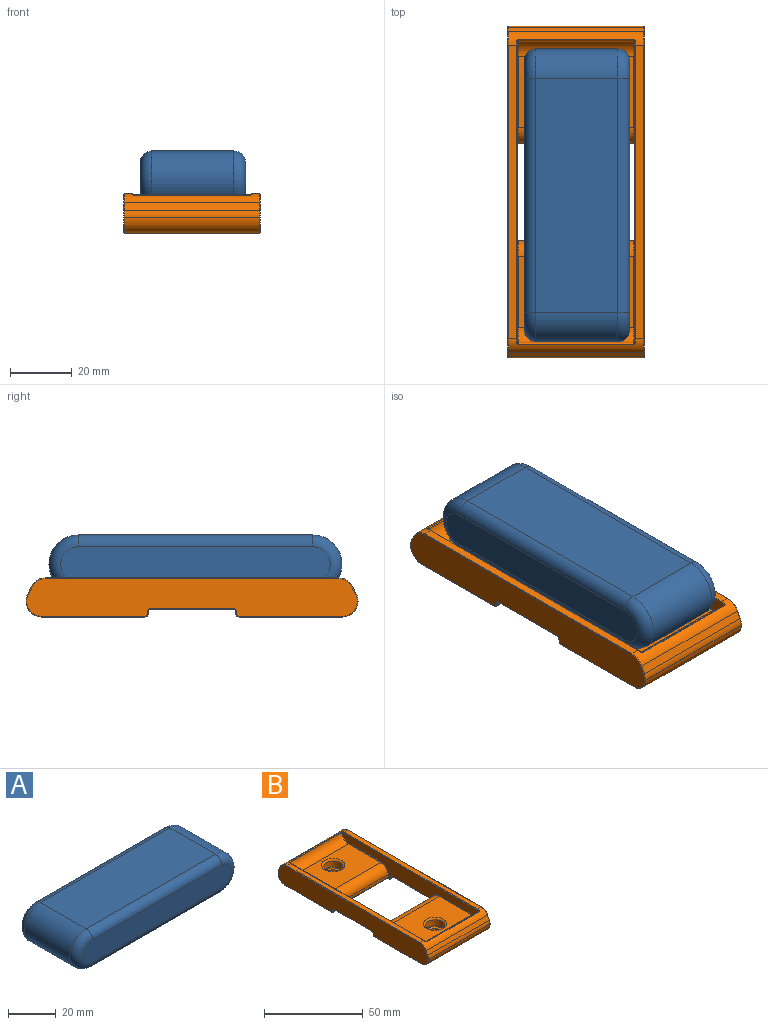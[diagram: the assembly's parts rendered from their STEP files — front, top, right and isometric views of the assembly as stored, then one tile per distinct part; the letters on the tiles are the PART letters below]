
ASSEMBLY  parts=2 mates=3
PART A: 14 faces, bbox 96.8x34.3x20.6 mm
  f0: plane 76.2x26.67mm, normal (0,0,1), area 2032.3mm2, adj f1,f3,f6,f10
  f1: cylinder r=9.53mm len=26.67mm, axis (0,1,0), area 798.1mm2, adj f0,f2,f8,f12
  f2: plane 76.2x26.67mm, normal (0,0,-1), area 2032.3mm2, adj f1,f3,f9,f13
  f3: cylinder r=9.53mm len=26.67mm, axis (0,1,0), area 798.1mm2, adj f0,f2,f7,f11
  f4: plane 87.63x11.43mm, normal (0,-1,0), area 973.6mm2, adj f10,f11,f12,f13
  f5: plane 87.63x11.43mm, normal (0,1,0), area 973.6mm2, adj f6,f7,f8,f9
  f6: cylinder r=3.81mm len=76.2mm, axis (-1,0,0), area 456mm2, adj f0,f5,f7,f8
  f7: torus R=5.71mm, axis (0,-1,0), area 153.1mm2, adj f3,f5,f6,f9
  f8: torus R=5.71mm, axis (0,-1,0), area 153.1mm2, adj f1,f5,f6,f9
  f9: cylinder r=3.81mm len=76.2mm, axis (1,0,0), area 456mm2, adj f2,f5,f7,f8
  f10: cylinder r=3.81mm len=76.2mm, axis (1,0,0), area 456mm2, adj f0,f4,f11,f12
  f11: torus R=5.71mm, axis (0,-1,0), area 153.1mm2, adj f3,f4,f10,f13
  f12: torus R=5.71mm, axis (0,-1,0), area 153.1mm2, adj f1,f4,f10,f13
  f13: cylinder r=3.81mm len=76.2mm, axis (-1,0,0), area 456mm2, adj f2,f4,f11,f12
PART B: 148 faces, bbox 44.5x108.8x13.7 mm
  f0: plane 95.32x2.67mm, normal (0,0,1), area 254.2mm2, adj f35,f36,f50,f124
  f1: plane 37.59x23.18mm, normal (0,0,1), area 762.3mm2, adj f23,f31,f49,f103,f107
  f2: plane 2.67x0.51mm, normal (0,1,0), area 1.4mm2, adj f44,f46,f65,f139
  f3: plane 2.67x0.51mm, normal (0,-1,0), area 1.4mm2, adj f45,f47,f66,f131
  f4: plane 26.54x2.67mm, normal (0,0,-1), area 70.8mm2, adj f46,f47,f69,f135
  f5: plane 43.95x33.6mm, normal (0,0,-1), area 1383.9mm2, adj f32,f38,f40,f44,f61,f81,f102,f104
  f6: plane 107.44x12.19mm, normal (1,0,0), area 1204.4mm2, adj f50,f51,f52,f53,f54,f55,f56,f57
  f7: plane 95.32x2.67mm, normal (0,0,1), area 254.2mm2, adj f35,f36,f70,f117
  f8: plane 43.94x0.07mm, normal (0,-1,0), area 3.1mm2, adj f32,f37,f57,f77
  f9: plane 43.95x33.6mm, normal (0,0,-1), area 1383.9mm2, adj f33,f39,f41,f45,f62,f82,f93,f95
  f10: plane 43.94x0.07mm, normal (0,1,0), area 3.1mm2, adj f33,f34,f58,f78
  f11: plane 43.94x2.47mm, normal (0,0.89,0.45), area 121.3mm2, adj f34,f35,f54,f74
  f12: plane 43.94x2.47mm, normal (0,-0.89,0.45), area 121.3mm2, adj f36,f37,f53,f73
  f13: plane 107.44x12.19mm, normal (-1,0,0), area 1204.4mm2, adj f70,f71,f72,f73,f74,f75,f76,f77
  f14: plane 97.88x12.19mm, normal (-1,0,0), area 614.5mm2, adj f107,f110,f111,f115,f119,f120,f124,f126
  f15: plane 97.88x12.19mm, normal (1,0,0), area 614.5mm2, adj f90,f91,f92,f93,f94,f96,f97,f98
  f16: plane 37.59x23.18mm, normal (0,0,1), area 762.3mm2, adj f24,f30,f48,f118,f134
  f17: cylinder r=2.9mm len=5.8mm, axis (0,0,1), area 43.1mm2, adj f18,f145
  f18: plane 9.24x9.24mm, normal (0,0,1), area 40.7mm2, adj f17,f146
  f19: cylinder r=4.88mm len=9.75mm, axis (0,0,1), area 114.3mm2, adj f48,f146
  f20: cylinder r=2.9mm len=5.8mm, axis (0,0,1), area 43.1mm2, adj f21,f144
  f21: plane 9.24x9.24mm, normal (0,0,1), area 40.7mm2, adj f20,f147
  f22: cylinder r=4.88mm len=9.75mm, axis (0,0,1), area 114.3mm2, adj f49,f147
  f23: cylinder r=5.08mm len=37.59mm, axis (-1,0,0), area 278.7mm2, adj f1,f105,f111,f112
  f24: cylinder r=5.08mm len=37.59mm, axis (1,0,0), area 278.7mm2, adj f16,f122,f128,f132
  f25: plane 2.67x0.51mm, normal (0,1,0), area 1.4mm2, adj f40,f43,f85,f98
  f26: plane 2.67x0.51mm, normal (0,-1,0), area 1.4mm2, adj f41,f42,f86,f90
  f27: plane 26.54x2.67mm, normal (0,0,-1), area 70.8mm2, adj f42,f43,f89,f94
  f28: plane 37.59x1.52mm, normal (0,1,0), area 57.3mm2, adj f30,f38,f109,f138
  f29: plane 37.59x1.52mm, normal (0,-1,0), area 57.3mm2, adj f31,f39,f99,f115
  f30: cylinder r=5.08mm len=37.59mm, axis (-1,0,0), area 300mm2, adj f16,f28,f114,f136
  f31: cylinder r=5.08mm len=37.59mm, axis (1,0,0), area 300mm2, adj f1,f29,f101,f110
  f32: cylinder r=5.08mm len=43.94mm, axis (-1,0,0), area 350.6mm2, adj f5,f8,f59,f79
  f33: cylinder r=5.08mm len=43.94mm, axis (-1,0,0), area 350.6mm2, adj f9,f10,f60,f80
  f34: cylinder r=5.08mm len=43.94mm, axis (-1,0,0), area 103.5mm2, adj f10,f11,f56,f76
  f35: cylinder r=5.08mm len=43.94mm, axis (-1,0,0), area 173.5mm2, adj f0,f7,f11,f52,f72,f108,f112,f113
  f36: cylinder r=5.08mm len=43.94mm, axis (-1,0,0), area 173.5mm2, adj f0,f7,f12,f51,f71,f121,f125,f127
  f37: cylinder r=5.08mm len=43.94mm, axis (-1,0,0), area 103.5mm2, adj f8,f12,f55,f75
  f38: cylinder r=1.02mm len=37.59mm, axis (1,0,0), area 60mm2, adj f5,f28,f106,f140
  f39: cylinder r=1.02mm len=37.59mm, axis (-1,0,0), area 60mm2, adj f9,f29,f97,f119
  f40: cylinder r=1.02mm len=2.67mm, axis (-1,0,0), area 4.3mm2, adj f5,f25,f83,f100
  f41: cylinder r=1.02mm len=2.67mm, axis (1,0,0), area 4.3mm2, adj f9,f26,f84,f91
  f42: cylinder r=1.02mm len=2.67mm, axis (1,0,0), area 4.3mm2, adj f26,f27,f88,f92
  f43: cylinder r=1.02mm len=2.67mm, axis (-1,0,0), area 4.3mm2, adj f25,f27,f87,f96
  f44: cylinder r=1.02mm len=2.67mm, axis (-1,0,0), area 4.3mm2, adj f2,f5,f63,f141
  f45: cylinder r=1.02mm len=2.67mm, axis (1,0,0), area 4.3mm2, adj f3,f9,f64,f129
  f46: cylinder r=1.02mm len=2.67mm, axis (-1,0,0), area 4.3mm2, adj f2,f4,f67,f137
  f47: cylinder r=1.02mm len=2.67mm, axis (1,0,0), area 4.3mm2, adj f3,f4,f68,f133
  f48: torus R=5.89mm, axis (0,0,1), area 52.6mm2, adj f16,f19
  f49: torus R=5.89mm, axis (0,0,1), area 52.6mm2, adj f1,f22
  f50: cylinder r=0.25mm len=95.32mm, axis (0,1,0), area 38mm2, adj f0,f6,f51,f52
  f51: torus R=4.83mm, axis (1,0,0), area 2.2mm2, adj f6,f36,f50,f53
  f52: torus R=4.83mm, axis (1,0,0), area 2.2mm2, adj f6,f35,f50,f54
  f53: cylinder r=0.25mm len=2.58mm, axis (0,0.45,0.89), area 1.1mm2, adj f6,f12,f51,f55
  f54: cylinder r=0.25mm len=2.58mm, axis (0,0.45,-0.89), area 1.1mm2, adj f6,f11,f52,f56
  f55: torus R=4.83mm, axis (1,0,0), area 0.9mm2, adj f6,f37,f53,f57
  f56: torus R=4.83mm, axis (1,0,0), area 0.9mm2, adj f6,f34,f54,f58
  f57: cylinder r=0.25mm len=0.25mm, axis (0,0,1), area 0mm2, adj f6,f8,f55,f59
  f58: cylinder r=0.25mm len=0.25mm, axis (0,0,-1), area 0mm2, adj f6,f10,f56,f60
  f59: torus R=4.83mm, axis (1,0,0), area 3.1mm2, adj f6,f32,f57,f61
  f60: torus R=4.83mm, axis (1,0,0), area 3.1mm2, adj f6,f33,f58,f62
  f61: cylinder r=0.25mm len=33.59mm, axis (0,-1,0), area 13.4mm2, adj f5,f6,f59,f63
  f62: cylinder r=0.25mm len=33.59mm, axis (0,-1,0), area 13.4mm2, adj f6,f9,f60,f64
  f63: torus R=0.76mm, axis (1,0,0), area 0.6mm2, adj f6,f44,f61,f65
  f64: torus R=0.76mm, axis (1,0,0), area 0.6mm2, adj f6,f45,f62,f66
  f65: cylinder r=0.25mm len=0.51mm, axis (0,0,1), area 0.2mm2, adj f2,f6,f63,f67
  f66: cylinder r=0.25mm len=0.51mm, axis (0,0,-1), area 0.2mm2, adj f3,f6,f64,f68
  f67: torus R=1.27mm, axis (1,0,0), area 0.7mm2, adj f6,f46,f65,f69
  f68: torus R=1.27mm, axis (1,0,0), area 0.7mm2, adj f6,f47,f66,f69
  f69: cylinder r=0.25mm len=26.54mm, axis (0,1,0), area 10.6mm2, adj f4,f6,f67,f68
  f70: cylinder r=0.25mm len=95.32mm, axis (0,-1,0), area 38mm2, adj f7,f13,f71,f72
  f71: torus R=4.83mm, axis (1,0,0), area 2.2mm2, adj f13,f36,f70,f73
  f72: torus R=4.83mm, axis (1,0,0), area 2.2mm2, adj f13,f35,f70,f74
  f73: cylinder r=0.25mm len=2.58mm, axis (0,-0.45,-0.89), area 1.1mm2, adj f12,f13,f71,f75
  f74: cylinder r=0.25mm len=2.58mm, axis (0,-0.45,0.89), area 1.1mm2, adj f11,f13,f72,f76
  f75: torus R=4.83mm, axis (1,0,0), area 0.9mm2, adj f13,f37,f73,f77
  f76: torus R=4.83mm, axis (1,0,0), area 0.9mm2, adj f13,f34,f74,f78
  f77: cylinder r=0.25mm len=0.25mm, axis (0,0,-1), area 0mm2, adj f8,f13,f75,f79
  f78: cylinder r=0.25mm len=0.25mm, axis (0,0,1), area 0mm2, adj f10,f13,f76,f80
  f79: torus R=4.83mm, axis (1,0,0), area 3.1mm2, adj f13,f32,f77,f81
  f80: torus R=4.83mm, axis (1,0,0), area 3.1mm2, adj f13,f33,f78,f82
  f81: cylinder r=0.25mm len=33.59mm, axis (0,1,0), area 13.4mm2, adj f5,f13,f79,f83
  f82: cylinder r=0.25mm len=33.59mm, axis (0,1,0), area 13.4mm2, adj f9,f13,f80,f84
  f83: torus R=0.76mm, axis (1,0,0), area 0.6mm2, adj f13,f40,f81,f85
  f84: torus R=0.76mm, axis (1,0,0), area 0.6mm2, adj f13,f41,f82,f86
  f85: cylinder r=0.25mm len=0.51mm, axis (0,0,-1), area 0.2mm2, adj f13,f25,f83,f87
  f86: cylinder r=0.25mm len=0.51mm, axis (0,0,1), area 0.2mm2, adj f13,f26,f84,f88
  f87: torus R=1.27mm, axis (1,0,0), area 0.7mm2, adj f13,f43,f85,f89
  f88: torus R=1.27mm, axis (1,0,0), area 0.7mm2, adj f13,f42,f86,f89
  f89: cylinder r=0.25mm len=26.54mm, axis (0,-1,0), area 10.6mm2, adj f13,f27,f87,f88
  f90: cylinder r=0.25mm len=0.51mm, axis (0,0,1), area 0.2mm2, adj f15,f26,f91,f92
  f91: torus R=0.76mm, axis (-1,0,0), area 0.6mm2, adj f15,f41,f90,f93
  f92: torus R=1.27mm, axis (-1,0,0), area 0.7mm2, adj f15,f42,f90,f94
  f93: cylinder r=0.25mm len=0.57mm, axis (0,-1,0), area 0.2mm2, adj f9,f15,f91,f95
  f94: cylinder r=0.25mm len=26.54mm, axis (0,-1,0), area 10.6mm2, adj f15,f27,f92,f96
  f95: bspline ~1.19x0.51mm, area 0.2mm2, adj f9,f93,f97
  f96: torus R=1.27mm, axis (-1,0,0), area 0.7mm2, adj f15,f43,f94,f98
  f97: torus R=1.27mm, axis (-1,0,0), area 0.4mm2, adj f15,f39,f95,f99
  f98: cylinder r=0.25mm len=0.51mm, axis (0,0,-1), area 0.2mm2, adj f15,f25,f96,f100
  f99: cylinder r=0.25mm len=1.52mm, axis (0,0,1), area 0.6mm2, adj f15,f29,f97,f101
  f100: torus R=0.76mm, axis (-1,0,0), area 0.6mm2, adj f15,f40,f98,f102
  f101: torus R=5.33mm, axis (-1,0,0), area 3.2mm2, adj f15,f31,f99,f103
  f102: cylinder r=0.25mm len=0.57mm, axis (0,-1,0), area 0.2mm2, adj f5,f15,f100,f104
  f103: cylinder r=0.25mm len=23.18mm, axis (0,-1,0), area 9.2mm2, adj f1,f15,f101,f105
  f104: bspline ~1.19x0.51mm, area 0.2mm2, adj f5,f102,f106
  f105: torus R=4.83mm, axis (-1,0,0), area 2.9mm2, adj f15,f23,f103,f108
  f106: torus R=1.27mm, axis (-1,0,0), area 0.4mm2, adj f15,f38,f104,f109
  f107: cylinder r=0.25mm len=23.18mm, axis (0,1,0), area 9.2mm2, adj f1,f14,f110,f111
  f108: bspline ~0.64x0.6mm, area 0.2mm2, adj f35,f105,f112,f113
  f109: cylinder r=0.25mm len=1.52mm, axis (0,0,-1), area 0.6mm2, adj f15,f28,f106,f114
  f110: torus R=5.33mm, axis (-1,0,0), area 3.2mm2, adj f14,f31,f107,f115
  f111: torus R=4.83mm, axis (-1,0,0), area 2.9mm2, adj f14,f23,f107,f116
  f112: cylinder r=0.25mm len=37.59mm, axis (1,0,0), area 17.5mm2, adj f23,f35,f108,f116
  f113: torus R=4.83mm, axis (-1,0,0), area 0.5mm2, adj f15,f35,f108,f117
  f114: torus R=5.33mm, axis (-1,0,0), area 3.2mm2, adj f15,f30,f109,f118
  f115: cylinder r=0.25mm len=1.52mm, axis (0,0,-1), area 0.6mm2, adj f14,f29,f110,f119
  f116: bspline ~0.63x0.62mm, area 0.2mm2, adj f35,f111,f112,f120
  f117: cylinder r=0.25mm len=95.32mm, axis (0,-1,0), area 38mm2, adj f7,f15,f113,f121
  f118: cylinder r=0.25mm len=23.18mm, axis (0,-1,0), area 9.2mm2, adj f15,f16,f114,f122
  f119: torus R=1.27mm, axis (-1,0,0), area 0.4mm2, adj f14,f39,f115,f123
  f120: torus R=4.83mm, axis (-1,0,0), area 0.5mm2, adj f14,f35,f116,f124
  f121: torus R=4.83mm, axis (-1,0,0), area 0.5mm2, adj f15,f36,f117,f125
  f122: torus R=4.83mm, axis (-1,0,0), area 2.9mm2, adj f15,f24,f118,f125
  f123: bspline ~1.19x0.51mm, area 0.2mm2, adj f9,f119,f126
  f124: cylinder r=0.25mm len=95.32mm, axis (0,1,0), area 38mm2, adj f0,f14,f120,f127
  f125: bspline ~0.63x0.62mm, area 0.2mm2, adj f36,f121,f122,f128
  f126: cylinder r=0.25mm len=0.57mm, axis (0,1,0), area 0.2mm2, adj f9,f14,f123,f129
  f127: torus R=4.83mm, axis (-1,0,0), area 0.5mm2, adj f14,f36,f124,f130
  f128: cylinder r=0.25mm len=37.59mm, axis (-1,0,0), area 17.5mm2, adj f24,f36,f125,f130
  f129: torus R=0.76mm, axis (-1,0,0), area 0.6mm2, adj f14,f45,f126,f131
  f130: bspline ~0.64x0.6mm, area 0.2mm2, adj f36,f127,f128,f132
  f131: cylinder r=0.25mm len=0.51mm, axis (0,0,-1), area 0.2mm2, adj f3,f14,f129,f133
  f132: torus R=4.83mm, axis (-1,0,0), area 2.9mm2, adj f14,f24,f130,f134
  f133: torus R=1.27mm, axis (-1,0,0), area 0.7mm2, adj f14,f47,f131,f135
  f134: cylinder r=0.25mm len=23.18mm, axis (0,1,0), area 9.2mm2, adj f14,f16,f132,f136
  f135: cylinder r=0.25mm len=26.54mm, axis (0,1,0), area 10.6mm2, adj f4,f14,f133,f137
  f136: torus R=5.33mm, axis (-1,0,0), area 3.2mm2, adj f14,f30,f134,f138
  f137: torus R=1.27mm, axis (-1,0,0), area 0.7mm2, adj f14,f46,f135,f139
  f138: cylinder r=0.25mm len=1.52mm, axis (0,0,1), area 0.6mm2, adj f14,f28,f136,f140
  f139: cylinder r=0.25mm len=0.51mm, axis (0,0,1), area 0.2mm2, adj f2,f14,f137,f141
  f140: torus R=1.27mm, axis (-1,0,0), area 0.4mm2, adj f14,f38,f138,f142
  f141: torus R=0.76mm, axis (-1,0,0), area 0.6mm2, adj f14,f44,f139,f143
  f142: bspline ~1.19x0.51mm, area 0.2mm2, adj f5,f140,f143
  f143: cylinder r=0.25mm len=0.57mm, axis (0,1,0), area 0.2mm2, adj f5,f14,f141,f142
  f144: torus R=3.15mm, axis (0,0,1), area 7.5mm2, adj f9,f20
  f145: torus R=3.15mm, axis (0,0,1), area 7.5mm2, adj f5,f17
  f146: torus R=4.62mm, axis (0,0,1), area 12mm2, adj f18,f19
  f147: torus R=4.62mm, axis (0,0,1), area 12mm2, adj f21,f22
PLACE A rot(axis=(0,0,1),90deg) t=(0.08,-1.14,10.99)mm
PLACE B t=(-0.23,-0.01,-6.15)mm fixed
MATE parallel A.f4 <-> B.f6  axis (1,0,0) through (17.23,-1.14,10.99)mm
MATE planar A.f2 <-> B.f16  axis (0,0,-1) through (13.42,-39.24,1.47)mm
MATE parallel A.f0 <-> B.f16  axis (0,0,1) through (13.42,-39.24,20.52)mm
